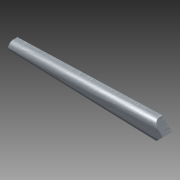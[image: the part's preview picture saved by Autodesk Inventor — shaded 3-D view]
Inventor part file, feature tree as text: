
AUTODESK INVENTOR PART (.ipt)
format: ipt  version: 2011 SP1 (Build 150282100, 282)  size: 89,088 bytes
history: native  units: in
note: dims shown in document units (in); Inventor stores cm internally (conversion verified against a paired STEP export)
features: extrude x1, fillet x1, sketch x1
ambient origin geometry x8: Origin, YZ Plane, XZ Plane, XY Plane, X Axis, Y Axis, Z Axis, Center Point
bodies: Solid1 (feature_tree)
feature tree (3):
  extrude  "Extrusion1"  Depth=0.25in
  fillet  "Fillet1"  Radius=0.25in
  sketch  "Sketch1"  dims[d0=4.0625in d1=0.25in d2=0.25in d5=0.25in d6=0.0in d7=0.15in d8=135.0deg]
